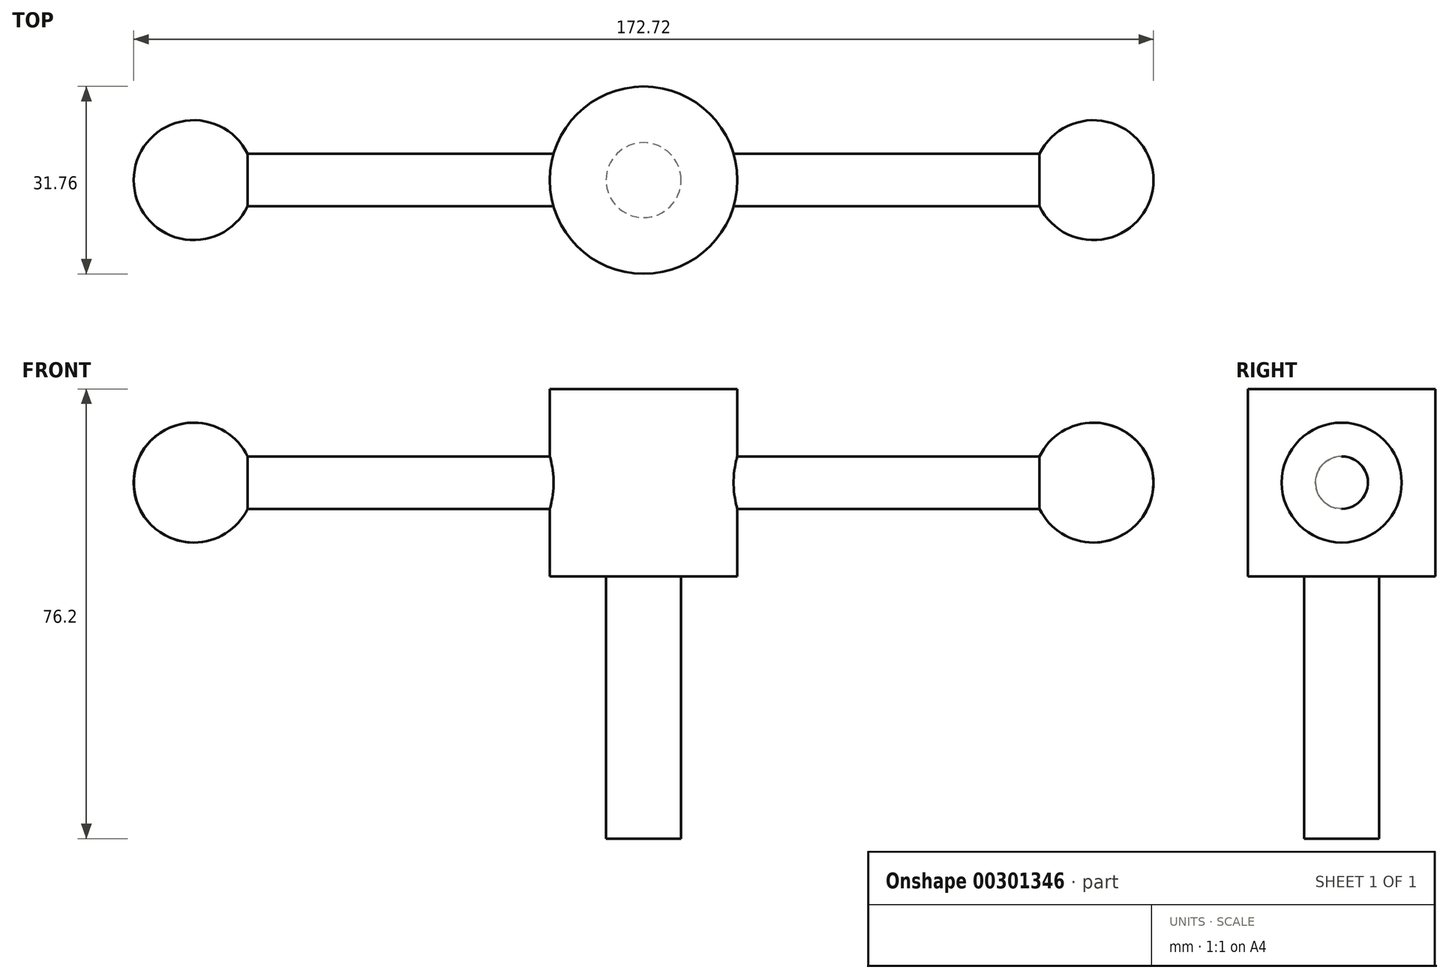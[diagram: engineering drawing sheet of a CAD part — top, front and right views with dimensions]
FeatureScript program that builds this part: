
annotation { "Feature Type Name" : "Feature", "Feature Type Description" : "" }
export const myFeature = defineFeature(function(context is Context, id is Id, definition is map)
    precondition{}
    {
        {
            var Q0;
            Q0=qCreatedBy(makeId("Top.planeOp"),FACE);
            var sketch = newSketch(context, id + "F0", { "sketchPlane" : qUnion([Q0])});
            skCircle(sketch, "E0", {"center": v(0, 0) * mm, "radius": 6.35 * mm});
            skSolve(sketch);
        }
        {
            var Q0;
            Q0 = qSketchRegion(id + "F0", true);
            extrude(context, id + "F1", {"entities" : qUnion([Q0]), "depth" : 44.45 * mm});
        }
        {
            var Q0;
            Q0=makeQuery(id+"F1.opExtrude","CAP_FACE",FACE,{"disambiguationData":[OSD([sQuery(id+"F0.wireOp",EDGE,"E0")])],"isStart":false});
            var sketch = newSketch(context, id + "F2", { "sketchPlane" : qUnion([Q0])});
            skCircle(sketch, "E1", {"center": v(0, 0) * mm, "radius": 15.88 * mm});
            skSolve(sketch);
        }
        {
            var Q0;
            Q0 = qSketchRegion(id + "F2", true);
            extrude(context, id + "F3", {"entities" : qUnion([Q0]), "operationType" : NewBodyOperationType.ADD, "depth" : 31.75 * mm});
        }
        {
            var Q0;
            Q0=qCreatedBy(makeId("Right.planeOp"),FACE);
            var sketch = newSketch(context, id + "F4", { "sketchPlane" : qUnion([Q0])});
            skCircle(sketch, "E2", {"center": v(0, 60.33) * mm, "radius": 4.45 * mm});
            skSolve(sketch);
        }
        {
            var Q0;
            Q0 = qSketchRegion(id + "F4", true);
            extrude(context, id + "F5", {"entities" : qUnion([Q0]), "operationType" : NewBodyOperationType.ADD, "depth" : 76.2 * mm, "hasSecondDirection" : true, "secondDirectionOppositeDirection" : true, "secondDirectionDepth" : 76.2 * mm});
        }
        {
            var Q0;
            Q0=qCreatedBy(makeId("Front.planeOp"),FACE);
            var sketch = newSketch(context, id + "F6", { "sketchPlane" : qUnion([Q0])});
            skLineSegment(sketch, "E3.0.0", {"start": v(76.2, 64.77) * mm, "end": v(76.2, 55.88) * mm});
            skArc(sketch, "E4", {"start": v(76.2, 70.48) * mm, "mid": v(66.04, 60.33) * mm, "end": v(76.2, 50.16) * mm});
            skLineSegment(sketch, "E5", {"start": v(76.2, 45.95) * mm, "end": v(76.2, 72.17) * mm});
            skLineSegment(sketch, "E6", {"start": v(76.2, 72.17) * mm, "end": v(76.2, 77.04) * mm, "construction": true});
            skSolve(sketch);
        }
        {
            var Q0;
            Q0 = qSketchRegion(id + "F6", true);
            var Q1;
            Q1=sQuery(id+"F6.wireOp",EDGE,"E6");
            revolve(context, id + "F7", {"operationType" : NewBodyOperationType.ADD, "entities" : qUnion([Q0]), "axis" : qUnion([Q1]), "revolveType" : RevolveType.FULL});
        }
        {
            var Q0;
            Q0=qCreatedBy(makeId("Front.planeOp"),FACE);
            var sketch = newSketch(context, id + "F8", { "sketchPlane" : qUnion([Q0])});
            skLineSegment(sketch, "E7.0.0", {"start": v(-76.2, 55.88) * mm, "end": v(-76.2, 64.77) * mm});
            skArc(sketch, "E8", {"start": v(-76.2, 50.16) * mm, "mid": v(-66.04, 60.33) * mm, "end": v(-76.2, 70.48) * mm});
            skLineSegment(sketch, "E9", {"start": v(-76.2, 72.93) * mm, "end": v(-76.2, 46.3) * mm});
            skLineSegment(sketch, "E10", {"start": v(-76.2, 46.3) * mm, "end": v(-76.2, 44.05) * mm, "construction": true});
            skSolve(sketch);
        }
        {
            var Q0;
            Q0 = qSketchRegion(id + "F8", true);
            var Q1;
            Q1=sQuery(id+"F8.wireOp",EDGE,"E10");
            revolve(context, id + "F9", {"operationType" : NewBodyOperationType.ADD, "entities" : qUnion([Q0]), "axis" : qUnion([Q1]), "revolveType" : RevolveType.FULL});
        }
    });
